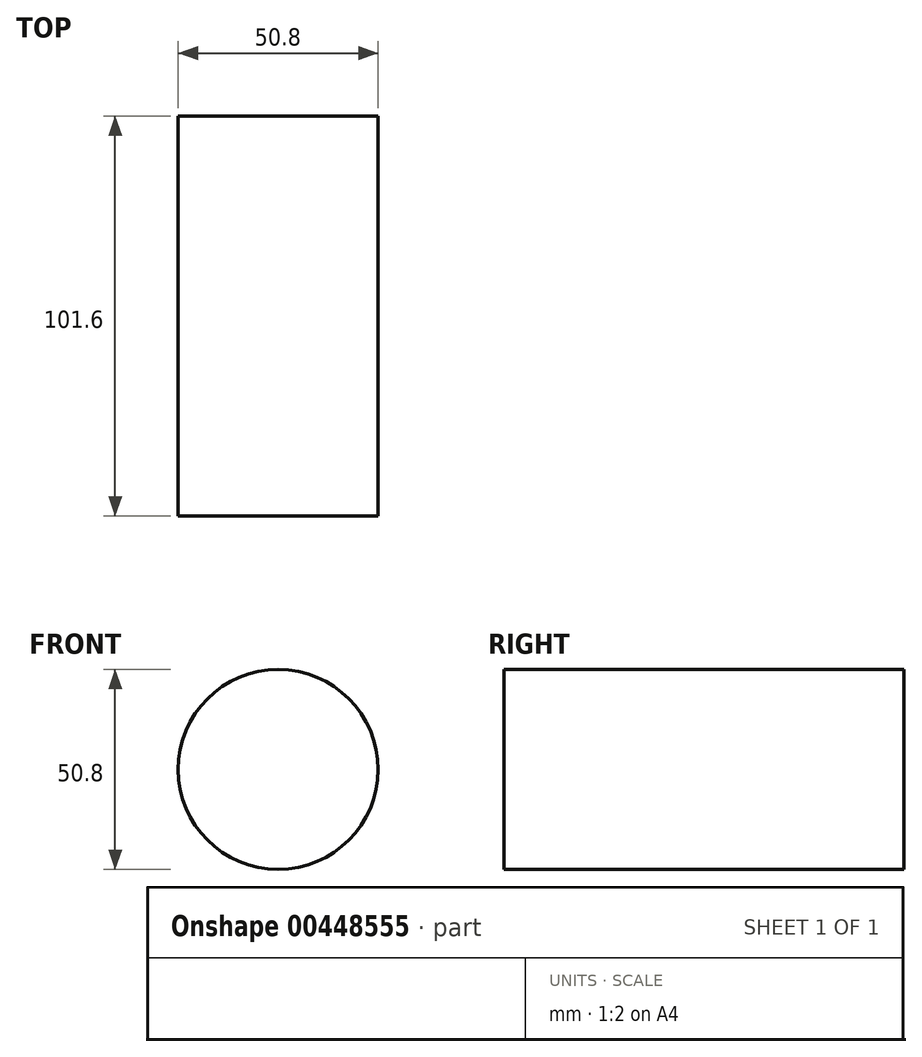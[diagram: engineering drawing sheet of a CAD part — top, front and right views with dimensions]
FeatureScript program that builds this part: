
annotation { "Feature Type Name" : "Feature", "Feature Type Description" : "" }
export const myFeature = defineFeature(function(context is Context, id is Id, definition is map)
    precondition{}
    {
        {
            var Q0;
            Q0=qCreatedBy(makeId("Front.planeOp"),FACE);
            var sketch = newSketch(context, id + "F0", { "sketchPlane" : qUnion([Q0])});
            skCircle(sketch, "E0", {"center": v(0, 0) * mm, "radius": 25.4 * mm});
            skSolve(sketch);
        }
        {
            var Q0;
            Q0=sQuery(id+"F0.wireOp",EDGE,"E0");
            extrude(context, id + "F1", {"bodyType" : ToolBodyType.SURFACE, "surfaceEntities" : qUnion([Q0]), "depth" : 101.6 * mm});
        }
    });
